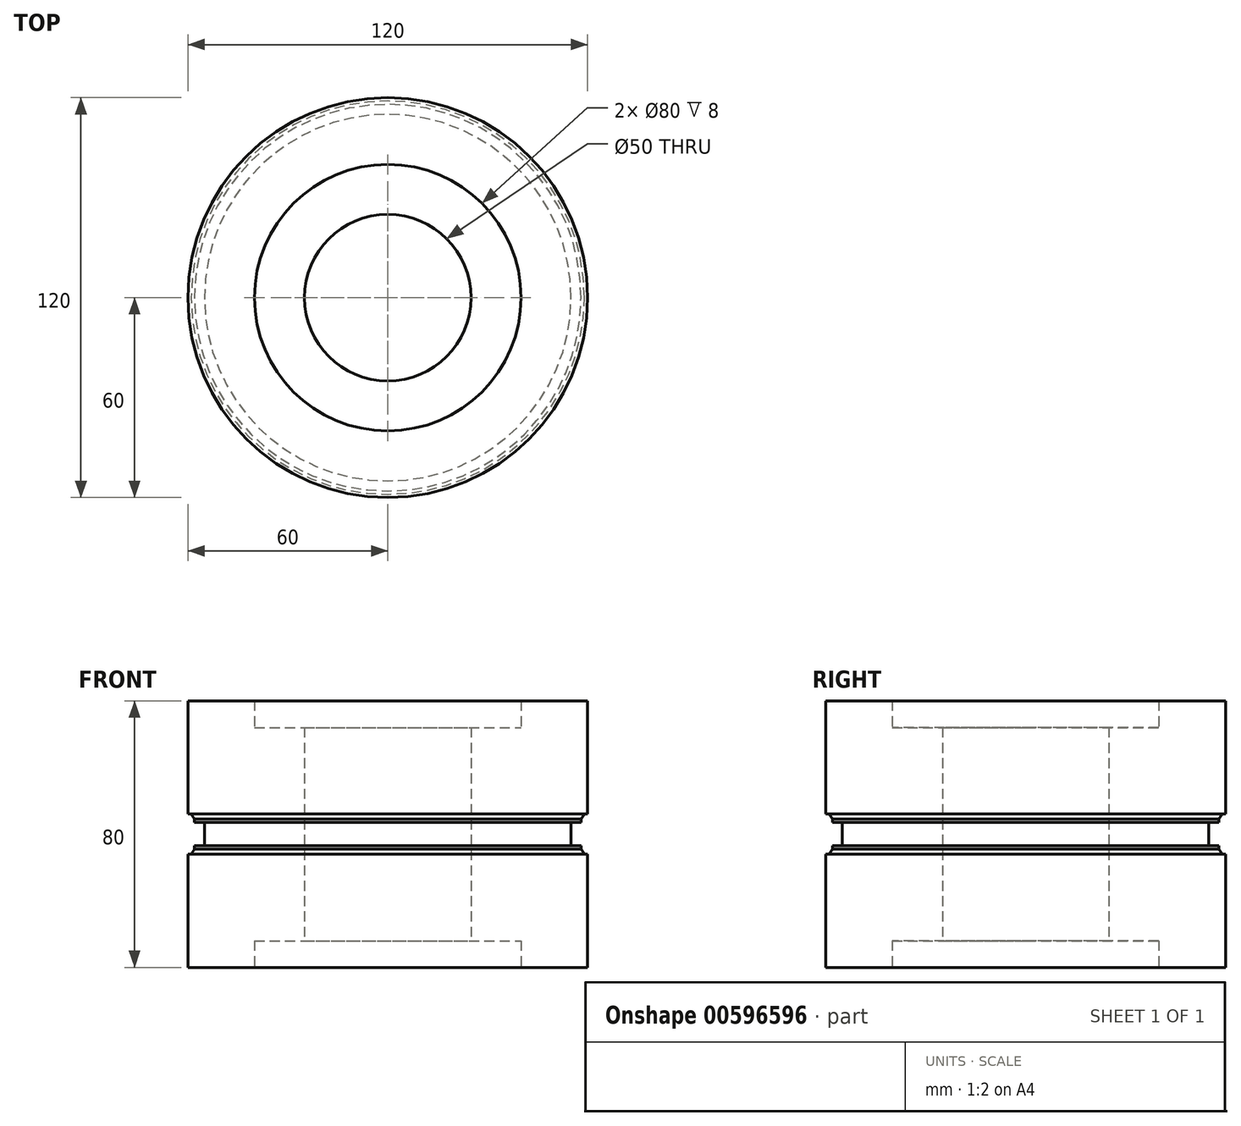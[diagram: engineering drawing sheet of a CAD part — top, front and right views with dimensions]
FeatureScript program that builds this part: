
annotation { "Feature Type Name" : "Feature", "Feature Type Description" : "" }
export const myFeature = defineFeature(function(context is Context, id is Id, definition is map)
    precondition{}
    {
        {
            var Q0;
            Q0=qCreatedBy(makeId("Front.planeOp"),FACE);
            var sketch = newSketch(context, id + "F0", { "sketchPlane" : qUnion([Q0])});
            skLineSegment(sketch, "E0", {"start": v(0, 8) * mm, "end": v(0, 72) * mm});
            skLineSegment(sketch, "E1", {"start": v(40, 80) * mm, "end": v(60, 80) * mm});
            skLineSegment(sketch, "E2", {"start": v(60, 80) * mm, "end": v(60, 46) * mm});
            skLineSegment(sketch, "E3", {"start": v(0, 40) * mm, "end": v(75.15, 40) * mm, "construction": true});
            skLineSegment(sketch, "E4.0", {"start": v(55, 36.5) * mm, "end": v(55, 43.5) * mm});
            skLineSegment(sketch, "E5.trimOffspring", {"start": v(59, 46) * mm, "end": v(60, 46) * mm});
            skLineSegment(sketch, "E6.0", {"start": v(55, 43.5) * mm, "end": v(58, 43.5) * mm});
            skLineSegment(sketch, "E7.0", {"start": v(58, 43.5) * mm, "end": v(58, 44.5) * mm});
            skLineSegment(sketch, "E8", {"start": v(59, 46) * mm, "end": v(58, 44.5) * mm});
            skLineSegment(sketch, "E9.MirrorCS", {"start": v(58, 36.5) * mm, "end": v(58, 35.5) * mm});
            skLineSegment(sketch, "E10.MirrorCS", {"start": v(60, 0) * mm, "end": v(60, 34) * mm});
            skLineSegment(sketch, "E11.MirrorCS", {"start": v(59, 34) * mm, "end": v(58, 35.5) * mm});
            skLineSegment(sketch, "E12.MirrorCS", {"start": v(59, 34) * mm, "end": v(60, 34) * mm});
            skLineSegment(sketch, "E13.MirrorCS", {"start": v(55, 36.5) * mm, "end": v(58, 36.5) * mm});
            skLineSegment(sketch, "E14", {"start": v(40, 0) * mm, "end": v(60, 0) * mm});
            skPoint(sketch, "E15.0.end.orphan", {"position": v(59, 80) * mm});
            skPoint(sketch, "E16.orphan", {"position": v(58, 80) * mm});
            skPoint(sketch, "E17.orphan", {"position": v(58, 0) * mm});
            skPoint(sketch, "E18.MirrorCS.end.orphan", {"position": v(59, 0) * mm});
            skPoint(sketch, "E18.MirrorCS.start.orphan", {"position": v(59, 34) * mm});
            skLineSegment(sketch, "E19.0", {"start": v(40, 0) * mm, "end": v(40, 8) * mm});
            skLineSegment(sketch, "E20.0", {"start": v(25, 72) * mm, "end": v(40, 72) * mm});
            skLineSegment(sketch, "E21.0", {"start": v(25, 8) * mm, "end": v(40, 8) * mm});
            skLineSegment(sketch, "E22.trimOffspring", {"start": v(40, 72) * mm, "end": v(40, 80) * mm});
            skPoint(sketch, "E23.orphan", {"position": v(0, 80) * mm});
            skPoint(sketch, "E24.orphan", {"position": v(0, 0) * mm});
            skLineSegment(sketch, "E25.0", {"start": v(25, 8) * mm, "end": v(25, 72) * mm});
            skSolve(sketch);
        }
        {
            var Q0;
            Q0 = qSketchRegion(id + "F0", true);
            var Q1;
            Q1=sQuery(id+"F0.wireOp",EDGE,"E0");
            revolve(context, id + "F1", {"entities" : qUnion([Q0]), "axis" : qUnion([Q1]), "revolveType" : RevolveType.FULL});
        }
    });
